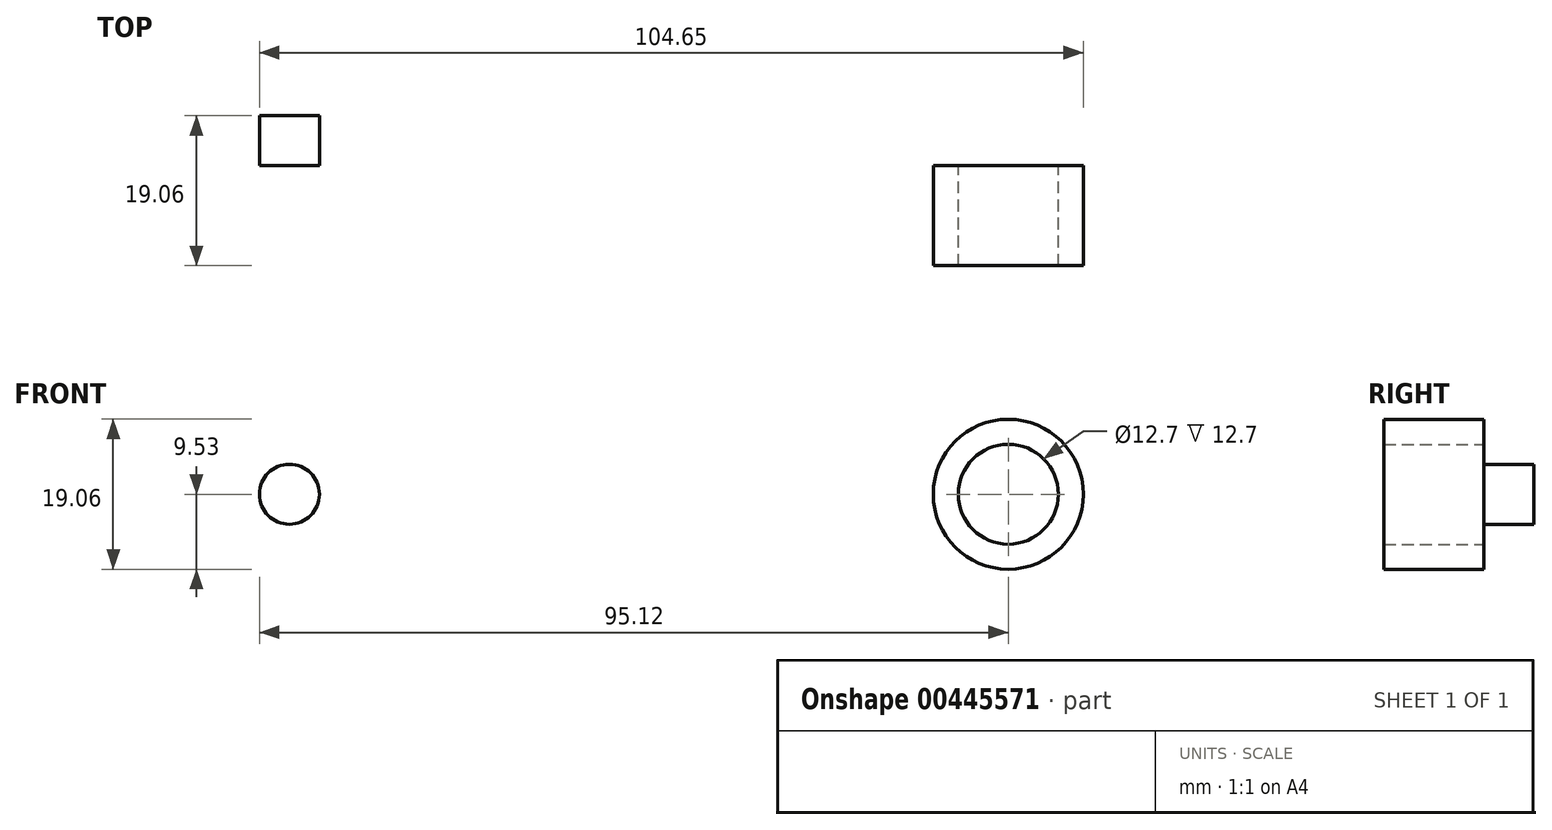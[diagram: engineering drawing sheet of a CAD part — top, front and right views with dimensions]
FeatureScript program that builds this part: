
annotation { "Feature Type Name" : "Feature", "Feature Type Description" : "" }
export const myFeature = defineFeature(function(context is Context, id is Id, definition is map)
    precondition{}
    {
        {
            var Q0;
            Q0=qCreatedBy(makeId("Front.planeOp"),FACE);
            var sketch = newSketch(context, id + "F0", { "sketchPlane" : qUnion([Q0])});
            skLineSegment(sketch, "E0.bottom", {"start": v(-101.6, 12.7) * mm, "end": v(101.6, 12.7) * mm});
            skLineSegment(sketch, "E0.top", {"start": v(-101.6, -12.7) * mm, "end": v(101.6, -12.7) * mm});
            skLineSegment(sketch, "E0.left", {"start": v(-101.6, 12.7) * mm, "end": v(-101.6, -12.7) * mm});
            skLineSegment(sketch, "E0.right", {"start": v(101.6, 12.7) * mm, "end": v(101.6, -12.7) * mm});
            skPoint(sketch, "E0.middle", {"position": v(0, 0) * mm});
            skSolve(sketch);
        }
        {
            var Q0;
            Q0=makeQuery(id+"F0.imprint","IMPRINT",FACE,{"disambiguationData":[TD([[makeQuery(id+"F0.imprint","IMPRINT",EDGE,{"derivedFrom":sQuery(id+"F0.wireOp",EDGE,"E0.bottom")}),-1.0]])]});
            extrude(context, id + "F1", {"entities" : qUnion([Q0]), "endBound" : BoundingType.SYMMETRIC, "depth" : 6.35 * mm});
        }
        {
            var Q0;
            Q0=makeQuery(id+"F1.opExtrude","CAP_FACE",FACE,{"disambiguationData":[OSD([sQuery(id+"F0.wireOp",EDGE,"E0.bottom"),sQuery(id+"F0.wireOp",EDGE,"E0.top"),sQuery(id+"F0.wireOp",EDGE,"E0.left"),sQuery(id+"F0.wireOp",EDGE,"E0.right")])],"isStart":false});
            var sketch = newSketch(context, id + "F2", { "sketchPlane" : qUnion([Q0])});
            skPoint(sketch, "E1.0", {"position": v(0, 0) * mm});
            skCircle(sketch, "E2", {"center": v(0, 0) * mm, "radius": 6.35 * mm});
            skCircle(sketch, "E3", {"center": v(0, 0) * mm, "radius": 9.53 * mm});
            skSolve(sketch);
        }
        {
            var Q0;
            Q0=makeQuery(id+"F2.imprint","IMPRINT",FACE,{"disambiguationData":[TD([[makeQuery(id+"F2.imprint","IMPRINT",EDGE,{"derivedFrom":sQuery(id+"F2.wireOp",EDGE,"E2")}),-1.0]])]});
            extrude(context, id + "F3", {"entities" : qUnion([Q0]), "depth" : 12.7 * mm});
        }
        {
            var Q0;
            Q0=makeQuery(id+"F1.opExtrude","CAP_FACE",FACE,{"disambiguationData":[OSD([sQuery(id+"F0.wireOp",EDGE,"E0.bottom"),sQuery(id+"F0.wireOp",EDGE,"E0.top"),sQuery(id+"F0.wireOp",EDGE,"E0.left"),sQuery(id+"F0.wireOp",EDGE,"E0.right")])],"isStart":false});
            var sketch = newSketch(context, id + "F4", { "sketchPlane" : qUnion([Q0])});
            skPoint(sketch, "E4.0", {"position": v(0, 0) * mm});
            skLineSegment(sketch, "E5", {"start": v(2.41, 0) * mm, "end": v(91.31, 0) * mm, "construction": true});
            skCircle(sketch, "E6", {"center": v(91.31, 0) * mm, "radius": 3.81 * mm});
            skCircle(sketch, "E7.MirrorC", {"center": v(-91.31, 0) * mm, "radius": 3.81 * mm});
            skSolve(sketch);
        }
        {
            var Q0;
            Q0=makeQuery(id+"F4.imprint","IMPRINT",FACE,{"disambiguationData":[TD([[makeQuery(id+"F4.imprint","IMPRINT",EDGE,{"derivedFrom":sQuery(id+"F4.wireOp",EDGE,"E7.MirrorC")}),-1.0]])]});
            var Q1;
            Q1=makeQuery(id+"F4.imprint","IMPRINT",FACE,{"disambiguationData":[TD([[makeQuery(id+"F4.imprint","IMPRINT",EDGE,{"derivedFrom":sQuery(id+"F4.wireOp",EDGE,"E6")}),1.0]])]});
            extrude(context, id + "F5", {"entities" : qUnion([Q0, Q1]), "operationType" : NewBodyOperationType.REMOVE, "endBound" : BoundingType.THROUGH_ALL, "oppositeDirection" : true, "depth" : 25.4 * mm});
        }
    });
